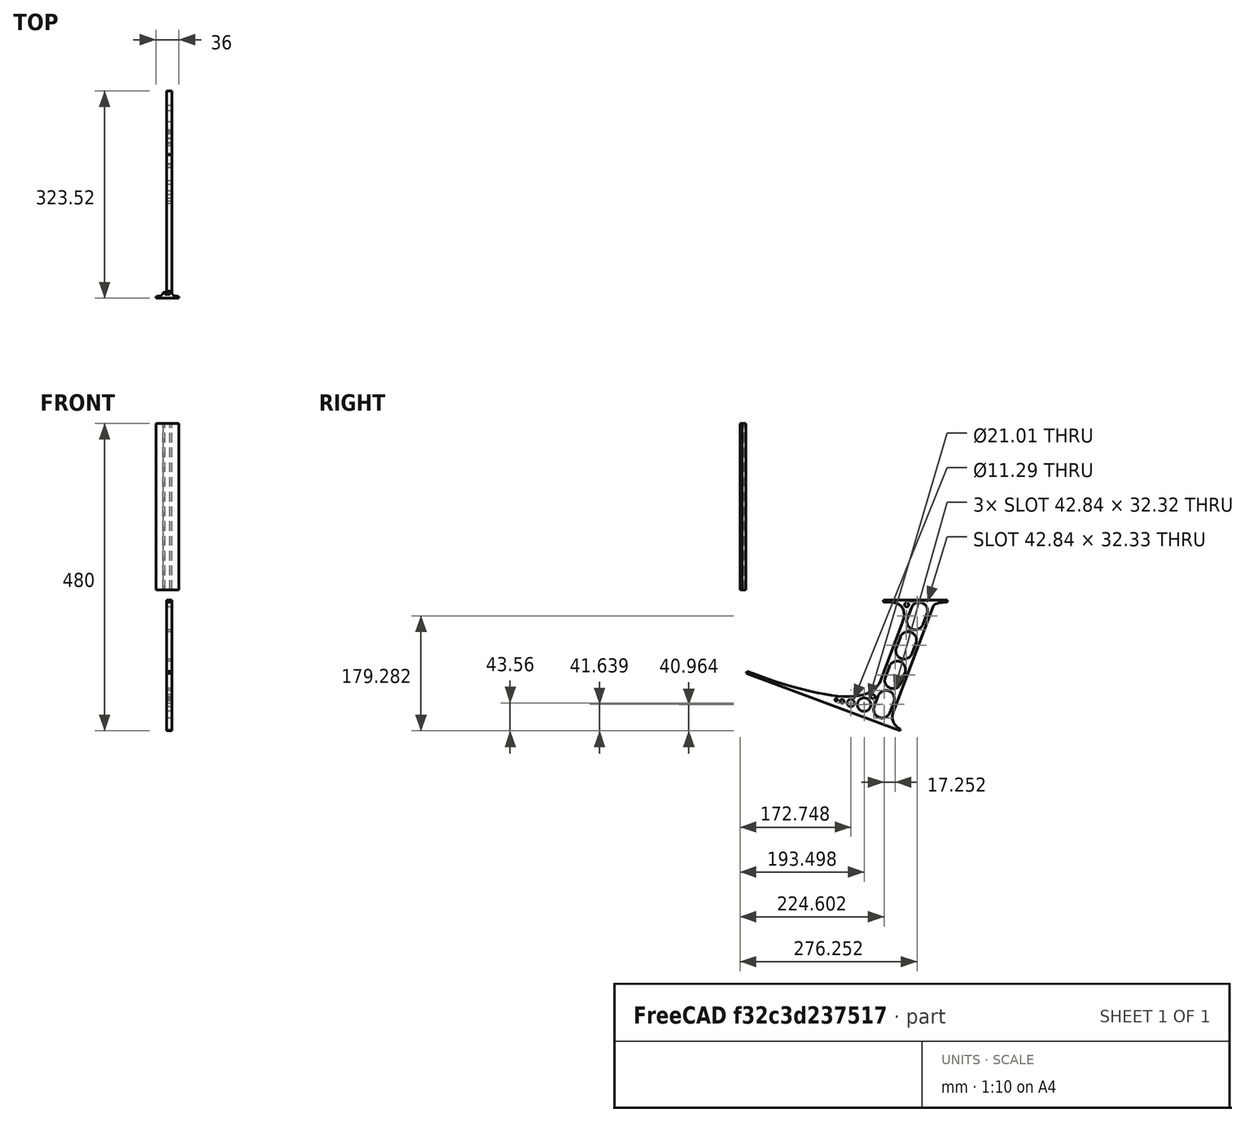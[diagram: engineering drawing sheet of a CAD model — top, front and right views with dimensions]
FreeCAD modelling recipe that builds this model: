
FCSTD DOCUMENT  (FreeCAD 0.19R0.19.2)
Label: laptopStand111
License: All rights reserved
LicenseURL: http://en.wikipedia.org/wiki/All_rights_reserved
objects: Sketcher::SketchObject×3, Part::Extrusion×3
note: 6 computed .brp shape members not serialized (recipe doc carries the construction recipe); baked Part::Feature solids carry a one-line shape summary decoded from their .brp

FEATURE [Sketcher::SketchObject] Sketch
  FullyConstrained = true
  sketch-geometry (316):
    g0: LineSegment StartX=-10.9272 StartY=-82.7794 StartZ=0 EndX=46.0728 EndY=-51.4823 EndZ=0
    g1: LineSegment StartX=-10.9272 StartY=77.3346 StartZ=0 EndX=-10.9272 EndY=-82.7794 EndZ=0
    g2: LineSegment StartX=-1.92719 StartY=-91.7794 StartZ=0 EndX=46.0728 EndY=-91.7794 EndZ=0
    g3: LineSegment StartX=318.073 StartY=-65.424 StartZ=0 EndX=318.073 EndY=-91.7794 EndZ=0
    g4: LineSegment StartX=318.073 StartY=-91.7794 StartZ=0 EndX=366.073 EndY=-91.7794 EndZ=0
    g5: LineSegment StartX=46.0728 StartY=-65.424 StartZ=0 EndX=-1.92719 EndY=-91.7794 EndZ=0
    g6: LineSegment StartX=46.0728 StartY=-65.424 StartZ=0 EndX=46.0728 EndY=-91.7794 EndZ=0
    g7: LineSegment StartX=46.0728 StartY=77.3346 StartZ=0 EndX=46.0728 EndY=-51.4823 EndZ=0
    g8: LineSegment StartX=-42.9272 StartY=136.221 StartZ=0 EndX=-42.9272 EndY=-103.779 EndZ=0
    g9: LineSegment StartX=407.073 StartY=136.221 StartZ=0 EndX=407.073 EndY=-103.779 EndZ=0
    g10: ArcOfCircle CenterX=-26.9272 CenterY=22.1087 CenterZ=0 NormalX=0 NormalY=0 NormalZ=1 AngleXU=0 Radius=8 StartAngle=1e-16 EndAngle=3.14159
    g11: ArcOfCircle CenterX=-26.9272 CenterY=-83.7794 CenterZ=0 NormalX=0 NormalY=0 NormalZ=1 AngleXU=0 Radius=8 StartAngle=3.14159 EndAngle=6.28319
    g12: LineSegment StartX=-34.9272 StartY=22.1087 StartZ=0 EndX=-34.9272 EndY=-83.7794 EndZ=0
    g13: LineSegment StartX=-18.9272 StartY=22.1087 StartZ=0 EndX=-18.9272 EndY=-83.7794 EndZ=0
    g14: ArcOfCircle CenterX=391.073 CenterY=22.1087 CenterZ=0 NormalX=0 NormalY=0 NormalZ=1 AngleXU=0 Radius=8 StartAngle=-4.4e-15 EndAngle=3.14159
    g15: LineSegment StartX=399.073 StartY=22.1087 StartZ=0 EndX=399.073 EndY=-83.7794 EndZ=0
    g16: LineSegment StartX=383.073 StartY=22.1087 StartZ=0 EndX=383.073 EndY=-83.7794 EndZ=0
    g17: ArcOfCircle CenterX=391.073 CenterY=-83.7794 CenterZ=0 NormalX=0 NormalY=0 NormalZ=1 AngleXU=0 Radius=8 StartAngle=3.14159 EndAngle=6.28319
    g18: Circle CenterX=175.022 CenterY=27.0628 CenterZ=0 NormalX=0 NormalY=0 NormalZ=1 AngleXU=0 Radius=1
    g19: Circle CenterX=179.022 CenterY=24.8665 CenterZ=0 NormalX=0 NormalY=0 NormalZ=1 AngleXU=0 Radius=1
    g20: Circle CenterX=179.022 CenterY=27.0628 CenterZ=0 NormalX=0 NormalY=0 NormalZ=1 AngleXU=0 Radius=1
    g21: BSplineCurve PolesCount=3 KnotsCount=2 Degree=2 IsPeriodic=0
    g22: GeomPoint X=175.022 Y=27.0628 Z=0
    g23: GeomPoint X=179.022 Y=27.0628 Z=0
    g24: Circle CenterX=189.124 CenterY=27.0628 CenterZ=0 NormalX=0 NormalY=0 NormalZ=1 AngleXU=0 Radius=1
    g25: Circle CenterX=185.124 CenterY=24.8665 CenterZ=0 NormalX=0 NormalY=0 NormalZ=1 AngleXU=0 Radius=1
    g26: Circle CenterX=185.124 CenterY=27.0628 CenterZ=0 NormalX=0 NormalY=0 NormalZ=1 AngleXU=0 Radius=1
    g27: BSplineCurve PolesCount=3 KnotsCount=2 Degree=2 IsPeriodic=0
    g28: GeomPoint X=189.124 Y=27.0628 Z=0
    g29: GeomPoint X=185.124 Y=27.0628 Z=0
    g30: Circle CenterX=175.022 CenterY=5.37834 CenterZ=0 NormalX=0 NormalY=0 NormalZ=1 AngleXU=0 Radius=1
    g31: Circle CenterX=179.022 CenterY=7.57463 CenterZ=0 NormalX=0 NormalY=0 NormalZ=1 AngleXU=0 Radius=1
    g32: Circle CenterX=179.022 CenterY=5.34704 CenterZ=0 NormalX=0 NormalY=0 NormalZ=1 AngleXU=0 Radius=1
    g33: BSplineCurve PolesCount=3 KnotsCount=2 Degree=2 IsPeriodic=0
    g34: GeomPoint X=175.022 Y=5.37834 Z=0
    g35: GeomPoint X=179.022 Y=5.34704 Z=0
    g36: Circle CenterX=189.124 CenterY=5.37834 CenterZ=0 NormalX=0 NormalY=0 NormalZ=1 AngleXU=0 Radius=1
    g37: Circle CenterX=185.124 CenterY=7.57463 CenterZ=0 NormalX=0 NormalY=0 NormalZ=1 AngleXU=0 Radius=1
    g38: Circle CenterX=185.124 CenterY=5.34704 CenterZ=0 NormalX=0 NormalY=0 NormalZ=1 AngleXU=0 Radius=1
    g39: BSplineCurve PolesCount=3 KnotsCount=2 Degree=2 IsPeriodic=0
    g40: GeomPoint X=189.124 Y=5.37834 Z=0
    g41: GeomPoint X=185.124 Y=5.34704 Z=0
    g42: Circle CenterX=165.871 CenterY=18.1458 CenterZ=0 NormalX=0 NormalY=0 NormalZ=1 AngleXU=0 Radius=1
    g43: Circle CenterX=169.377 CenterY=16.2206 CenterZ=0 NormalX=0 NormalY=0 NormalZ=1 AngleXU=0 Radius=1
    g44: Circle CenterX=165.871 CenterY=14.2954 CenterZ=0 NormalX=0 NormalY=0 NormalZ=1 AngleXU=0 Radius=1
    g45: BSplineCurve PolesCount=3 KnotsCount=2 Degree=2 IsPeriodic=0
    g46: GeomPoint X=165.871 Y=18.1458 Z=0
    g47: GeomPoint X=165.871 Y=14.2954 Z=0
    g48: Circle CenterX=198.275 CenterY=18.1458 CenterZ=0 NormalX=0 NormalY=0 NormalZ=1 AngleXU=0 Radius=1
    g49: Circle CenterX=194.768 CenterY=16.2206 CenterZ=0 NormalX=0 NormalY=0 NormalZ=1 AngleXU=0 Radius=1
    g50: Circle CenterX=198.275 CenterY=14.2954 CenterZ=0 NormalX=0 NormalY=0 NormalZ=1 AngleXU=0 Radius=1
    g51: BSplineCurve PolesCount=3 KnotsCount=2 Degree=2 IsPeriodic=0
    g52: GeomPoint X=198.275 Y=18.1458 Z=0
    g53: GeomPoint X=198.275 Y=14.2954 Z=0
    g54: LineSegment StartX=407.073 StartY=-103.779 StartZ=0 EndX=-42.9272 EndY=-103.779 EndZ=0
    g55: LineSegment StartX=407.073 StartY=136.221 StartZ=0 EndX=-42.9272 EndY=136.221 EndZ=0
    g56: LineSegment StartX=46.0728 StartY=77.3346 StartZ=0 EndX=-10.9272 EndY=77.3346 EndZ=0
    g57: LineSegment StartX=46.0728 StartY=105.865 StartZ=0 EndX=31.5028 EndY=105.865 EndZ=0
    g58: LineSegment StartX=46.0728 StartY=124.221 StartZ=0 EndX=46.0728 EndY=105.865 EndZ=0
    g59: LineSegment StartX=-1.92719 StartY=124.221 StartZ=0 EndX=31.5028 EndY=105.865 EndZ=0
    g60: LineSegment StartX=46.0728 StartY=124.221 StartZ=0 EndX=-1.92719 EndY=124.221 EndZ=0
    g61: Circle CenterX=125.607 CenterY=54.1951 CenterZ=0 NormalX=0 NormalY=0 NormalZ=1 AngleXU=0 Radius=1
    g62: Circle CenterX=139.632 CenterY=46.4944 CenterZ=0 NormalX=0 NormalY=0 NormalZ=1 AngleXU=0 Radius=1
    g63: Circle CenterX=127.326 CenterY=56.7187 CenterZ=0 NormalX=0 NormalY=0 NormalZ=1 AngleXU=0 Radius=1
    g64: BSplineCurve PolesCount=3 KnotsCount=2 Degree=2 IsPeriodic=0
    g65: GeomPoint X=125.607 Y=54.1951 Z=0
    g66: GeomPoint X=127.326 Y=56.7187 Z=0
    g67: Circle CenterX=236.821 CenterY=56.7187 CenterZ=0 NormalX=0 NormalY=0 NormalZ=1 AngleXU=0 Radius=1
    g68: Circle CenterX=224.513 CenterY=46.4944 CenterZ=0 NormalX=0 NormalY=0 NormalZ=1 AngleXU=0 Radius=1
    g69: Circle CenterX=238.538 CenterY=54.1951 CenterZ=0 NormalX=0 NormalY=0 NormalZ=1 AngleXU=0 Radius=1
    g70: BSplineCurve PolesCount=3 KnotsCount=2 Degree=2 IsPeriodic=0
    g71: GeomPoint X=236.821 Y=56.7187 Z=0
    g72: GeomPoint X=238.538 Y=54.1951 Z=0
    g73: Circle CenterX=238.538 CenterY=-21.7539 CenterZ=0 NormalX=0 NormalY=0 NormalZ=1 AngleXU=0 Radius=1
    g74: Circle CenterX=224.513 CenterY=-14.0532 CenterZ=0 NormalX=0 NormalY=0 NormalZ=1 AngleXU=0 Radius=1
    g75: Circle CenterX=236.821 CenterY=-24.2775 CenterZ=0 NormalX=0 NormalY=0 NormalZ=1 AngleXU=0 Radius=1
    g76: BSplineCurve PolesCount=3 KnotsCount=2 Degree=2 IsPeriodic=0
    g77: GeomPoint X=238.538 Y=-21.7539 Z=0
    g78: GeomPoint X=236.821 Y=-24.2775 Z=0
    g79: Circle CenterX=125.607 CenterY=-21.7539 CenterZ=0 NormalX=0 NormalY=0 NormalZ=1 AngleXU=0 Radius=1
    g80: Circle CenterX=139.632 CenterY=-14.0532 CenterZ=0 NormalX=0 NormalY=0 NormalZ=1 AngleXU=0 Radius=1
    g81: Circle CenterX=127.325 CenterY=-24.2775 CenterZ=0 NormalX=0 NormalY=0 NormalZ=1 AngleXU=0 Radius=1
    g82: BSplineCurve PolesCount=3 KnotsCount=2 Degree=2 IsPeriodic=0
    g83: GeomPoint X=125.607 Y=-21.7539 Z=0
    g84: GeomPoint X=127.325 Y=-24.2775 Z=0
    g85: Circle CenterX=302.996 CenterY=111.695 CenterZ=0 NormalX=0 NormalY=0 NormalZ=1 AngleXU=0 Radius=1
    g86: Circle CenterX=306.073 CenterY=114.251 CenterZ=0 NormalX=0 NormalY=0 NormalZ=1 AngleXU=0 Radius=1
    g87: Circle CenterX=306.073 CenterY=110.251 CenterZ=0 NormalX=0 NormalY=0 NormalZ=1 AngleXU=0 Radius=1
    g88: BSplineCurve PolesCount=3 KnotsCount=2 Degree=2 IsPeriodic=0
    g89: GeomPoint X=302.996 Y=111.695 Z=0
    g90: GeomPoint X=306.073 Y=110.251 Z=0
    g91: Circle CenterX=306.073 CenterY=95.2763 CenterZ=0 NormalX=0 NormalY=0 NormalZ=1 AngleXU=0 Radius=1
    g92: Circle CenterX=306.073 CenterY=91.2763 CenterZ=0 NormalX=0 NormalY=0 NormalZ=1 AngleXU=0 Radius=1
    g93: Circle CenterX=302.567 CenterY=89.3511 CenterZ=0 NormalX=0 NormalY=0 NormalZ=1 AngleXU=0 Radius=1
    g94: BSplineCurve PolesCount=3 KnotsCount=2 Degree=2 IsPeriodic=0
    g95: GeomPoint X=306.073 Y=95.2763 Z=0
    g96: GeomPoint X=302.567 Y=89.3511 Z=0
    g97: LineSegment StartX=306.073 StartY=110.251 StartZ=0 EndX=306.073 EndY=95.2763 EndZ=0
    g98: LineSegment StartX=302.996 StartY=111.695 StartZ=0 EndX=236.821 EndY=56.7187 EndZ=0
    g99: LineSegment StartX=238.538 StartY=54.1951 StartZ=0 EndX=302.567 EndY=89.3511 EndZ=0
    g100: Circle CenterX=61.1496 CenterY=111.695 CenterZ=0 NormalX=0 NormalY=0 NormalZ=1 AngleXU=0 Radius=1
    g101: Circle CenterX=58.0728 CenterY=114.251 CenterZ=0 NormalX=0 NormalY=0 NormalZ=1 AngleXU=0 Radius=1
    g102: Circle CenterX=58.0728 CenterY=110.251 CenterZ=0 NormalX=0 NormalY=0 NormalZ=1 AngleXU=0 Radius=1
    g103: BSplineCurve PolesCount=3 KnotsCount=2 Degree=2 IsPeriodic=0
    g104: GeomPoint X=61.1496 Y=111.695 Z=0
    g105: GeomPoint X=58.0728 Y=110.251 Z=0
    g106: Circle CenterX=61.5791 CenterY=89.3511 CenterZ=0 NormalX=0 NormalY=0 NormalZ=1 AngleXU=0 Radius=1
    g107: Circle CenterX=58.0728 CenterY=91.2763 CenterZ=0 NormalX=0 NormalY=0 NormalZ=1 AngleXU=0 Radius=1
    g108: Circle CenterX=58.0728 CenterY=95.2763 CenterZ=0 NormalX=0 NormalY=0 NormalZ=1 AngleXU=0 Radius=1
    g109: BSplineCurve PolesCount=3 KnotsCount=2 Degree=2 IsPeriodic=0
    g110: GeomPoint X=61.5791 Y=89.3511 Z=0
    g111: GeomPoint X=58.0728 Y=95.2763 Z=0
    g112: LineSegment StartX=58.0728 StartY=110.251 StartZ=0 EndX=58.0728 EndY=95.2763 EndZ=0
    g113: LineSegment StartX=61.1496 StartY=111.695 StartZ=0 EndX=127.326 EndY=56.7187 EndZ=0
    g114: LineSegment StartX=125.607 StartY=54.1951 StartZ=0 EndX=61.5791 EndY=89.3511 EndZ=0
    g115: Circle CenterX=61.5791 CenterY=-56.9099 CenterZ=0 NormalX=0 NormalY=0 NormalZ=1 AngleXU=0 Radius=1
    g116: Circle CenterX=58.0728 CenterY=-58.8351 CenterZ=0 NormalX=0 NormalY=0 NormalZ=1 AngleXU=0 Radius=1
    g117: Circle CenterX=58.0728 CenterY=-62.8351 CenterZ=0 NormalX=0 NormalY=0 NormalZ=1 AngleXU=0 Radius=1
    g118: BSplineCurve PolesCount=3 KnotsCount=2 Degree=2 IsPeriodic=0
    g119: GeomPoint X=61.5791 Y=-56.9099 Z=0
    g120: GeomPoint X=58.0728 Y=-62.8351 Z=0
    g121: Circle CenterX=58.0728 CenterY=-77.8102 CenterZ=0 NormalX=0 NormalY=0 NormalZ=1 AngleXU=0 Radius=1
    g122: Circle CenterX=58.0728 CenterY=-81.8102 CenterZ=0 NormalX=0 NormalY=0 NormalZ=1 AngleXU=0 Radius=1
    g123: Circle CenterX=61.1496 CenterY=-79.2541 CenterZ=0 NormalX=0 NormalY=0 NormalZ=1 AngleXU=0 Radius=1
    g124: BSplineCurve PolesCount=3 KnotsCount=2 Degree=2 IsPeriodic=0
    g125: GeomPoint X=58.0728 Y=-77.8102 Z=0
    g126: GeomPoint X=61.1496 Y=-79.2541 Z=0
    g127: LineSegment StartX=58.0728 StartY=-62.8351 StartZ=0 EndX=58.0728 EndY=-77.8102 EndZ=0
    g128: LineSegment StartX=61.1496 StartY=-79.2541 StartZ=0 EndX=127.325 EndY=-24.2775 EndZ=0
    g129: LineSegment StartX=125.607 StartY=-21.7539 StartZ=0 EndX=61.5791 EndY=-56.9099 EndZ=0
    g130: Circle CenterX=302.567 CenterY=-56.9099 CenterZ=0 NormalX=0 NormalY=0 NormalZ=1 AngleXU=0 Radius=1
    g131: Circle CenterX=306.073 CenterY=-58.8351 CenterZ=0 NormalX=0 NormalY=0 NormalZ=1 AngleXU=0 Radius=1
    g132: Circle CenterX=306.073 CenterY=-62.8351 CenterZ=0 NormalX=0 NormalY=0 NormalZ=1 AngleXU=0 Radius=1
    g133: BSplineCurve PolesCount=3 KnotsCount=2 Degree=2 IsPeriodic=0
    g134: GeomPoint X=302.567 Y=-56.9099 Z=0
    g135: GeomPoint X=306.073 Y=-62.8351 Z=0
    g136: Circle CenterX=302.996 CenterY=-79.2541 CenterZ=0 NormalX=0 NormalY=0 NormalZ=1 AngleXU=0 Radius=1
    g137: Circle CenterX=306.073 CenterY=-81.8102 CenterZ=0 NormalX=0 NormalY=0 NormalZ=1 AngleXU=0 Radius=1
    g138: Circle CenterX=306.073 CenterY=-77.8102 CenterZ=0 NormalX=0 NormalY=0 NormalZ=1 AngleXU=0 Radius=1
    g139: BSplineCurve PolesCount=3 KnotsCount=2 Degree=2 IsPeriodic=0
    g140: GeomPoint X=302.996 Y=-79.2541 Z=0
    g141: GeomPoint X=306.073 Y=-77.8102 Z=0
    g142: LineSegment StartX=306.073 StartY=-62.8351 StartZ=0 EndX=306.073 EndY=-77.8102 EndZ=0
    g143: LineSegment StartX=302.996 StartY=-79.2541 StartZ=0 EndX=236.821 EndY=-24.2775 EndZ=0
    g144: LineSegment StartX=238.538 StartY=-21.7539 StartZ=0 EndX=302.567 EndY=-56.9099 EndZ=0
    g145: Circle CenterX=61.6457 CenterY=-88.8112 CenterZ=0 NormalX=0 NormalY=0 NormalZ=1 AngleXU=0 Radius=1
    g146: Circle CenterX=58.0728 CenterY=-91.7794 CenterZ=0 NormalX=0 NormalY=0 NormalZ=1 AngleXU=0 Radius=1
    g147: Circle CenterX=63.9135 CenterY=-91.7794 CenterZ=0 NormalX=0 NormalY=0 NormalZ=1 AngleXU=0 Radius=1
    g148: BSplineCurve PolesCount=3 KnotsCount=2 Degree=2 IsPeriodic=0
    g149: GeomPoint X=61.6457 Y=-88.8112 Z=0
    g150: GeomPoint X=63.9135 Y=-91.7794 Z=0
    g151: Circle CenterX=179.022 CenterY=-85.8163 CenterZ=0 NormalX=0 NormalY=0 NormalZ=1 AngleXU=0 Radius=1
    g152: Circle CenterX=179.022 CenterY=-91.7794 CenterZ=0 NormalX=0 NormalY=0 NormalZ=1 AngleXU=0 Radius=1
    g153: Circle CenterX=171.895 CenterY=-91.7794 CenterZ=0 NormalX=0 NormalY=0 NormalZ=1 AngleXU=0 Radius=1
    g154: BSplineCurve PolesCount=3 KnotsCount=2 Degree=2 IsPeriodic=0
    g155: GeomPoint X=179.022 Y=-85.8163 Z=0
    g156: GeomPoint X=171.895 Y=-91.7794 Z=0
    g157: Circle CenterX=185.124 CenterY=-86.2028 CenterZ=0 NormalX=0 NormalY=0 NormalZ=1 AngleXU=0 Radius=1
    g158: Circle CenterX=185.124 CenterY=-91.7794 CenterZ=0 NormalX=0 NormalY=0 NormalZ=1 AngleXU=0 Radius=1
    g159: Circle CenterX=191.747 CenterY=-91.7794 CenterZ=0 NormalX=0 NormalY=0 NormalZ=1 AngleXU=0 Radius=1
    g160: BSplineCurve PolesCount=3 KnotsCount=2 Degree=2 IsPeriodic=0
    g161: GeomPoint X=185.124 Y=-86.2028 Z=0
    g162: GeomPoint X=191.747 Y=-91.7794 Z=0
    g163: Circle CenterX=299.888 CenterY=-86.6413 CenterZ=0 NormalX=0 NormalY=0 NormalZ=1 AngleXU=0 Radius=1
    g164: Circle CenterX=306.073 CenterY=-91.7794 CenterZ=0 NormalX=0 NormalY=0 NormalZ=1 AngleXU=0 Radius=1
    g165: Circle CenterX=298.776 CenterY=-91.7794 CenterZ=0 NormalX=0 NormalY=0 NormalZ=1 AngleXU=0 Radius=1
    g166: BSplineCurve PolesCount=3 KnotsCount=2 Degree=2 IsPeriodic=0
    g167: GeomPoint X=299.888 Y=-86.6413 Z=0
    g168: GeomPoint X=298.776 Y=-91.7794 Z=0
    g169: LineSegment StartX=189.124 StartY=5.37834 StartZ=0 EndX=299.888 EndY=-86.6413 EndZ=0
    g170: LineSegment StartX=298.776 StartY=-91.7794 StartZ=0 EndX=191.747 EndY=-91.7794 EndZ=0
    g171: LineSegment StartX=185.124 StartY=-86.2028 StartZ=0 EndX=185.124 EndY=5.34704 EndZ=0
    g172: LineSegment StartX=179.022 StartY=5.34704 StartZ=0 EndX=179.022 EndY=-85.8163 EndZ=0
    g173: LineSegment StartX=171.895 StartY=-91.7794 StartZ=0 EndX=63.9135 EndY=-91.7794 EndZ=0
    g174: LineSegment StartX=61.6457 StartY=-88.8112 StartZ=0 EndX=175.022 EndY=5.37834 EndZ=0
    g175: Circle CenterX=302.073 CenterY=124.221 CenterZ=0 NormalX=0 NormalY=0 NormalZ=1 AngleXU=0 Radius=1
    g176: Circle CenterX=306.073 CenterY=124.221 CenterZ=0 NormalX=0 NormalY=0 NormalZ=1 AngleXU=0 Radius=1
    g177: Circle CenterX=302.996 CenterY=121.665 CenterZ=0 NormalX=0 NormalY=0 NormalZ=1 AngleXU=0 Radius=1
    g178: BSplineCurve PolesCount=3 KnotsCount=2 Degree=2 IsPeriodic=0
    g179: GeomPoint X=302.073 Y=124.221 Z=0
    g180: GeomPoint X=302.996 Y=121.665 Z=0
    g181: Circle CenterX=189.124 CenterY=124.221 CenterZ=0 NormalX=0 NormalY=0 NormalZ=1 AngleXU=0 Radius=1
    g182: Circle CenterX=185.124 CenterY=124.221 CenterZ=0 NormalX=0 NormalY=0 NormalZ=1 AngleXU=0 Radius=1
    g183: Circle CenterX=185.124 CenterY=120.221 CenterZ=0 NormalX=0 NormalY=0 NormalZ=1 AngleXU=0 Radius=1
    g184: BSplineCurve PolesCount=3 KnotsCount=2 Degree=2 IsPeriodic=0
    g185: GeomPoint X=189.124 Y=124.221 Z=0
    g186: GeomPoint X=185.124 Y=120.221 Z=0
    g187: Circle CenterX=175.022 CenterY=124.221 CenterZ=0 NormalX=0 NormalY=0 NormalZ=1 AngleXU=0 Radius=1
    g188: Circle CenterX=179.022 CenterY=124.221 CenterZ=0 NormalX=0 NormalY=0 NormalZ=1 AngleXU=0 Radius=1
    g189: Circle CenterX=179.022 CenterY=120.221 CenterZ=0 NormalX=0 NormalY=0 NormalZ=1 AngleXU=0 Radius=1
    g190: BSplineCurve PolesCount=3 KnotsCount=2 Degree=2 IsPeriodic=0
    g191: GeomPoint X=175.022 Y=124.221 Z=0
    g192: GeomPoint X=179.022 Y=120.221 Z=0
    g193: Circle CenterX=62.0728 CenterY=124.221 CenterZ=0 NormalX=0 NormalY=0 NormalZ=1 AngleXU=0 Radius=1
    g194: Circle CenterX=58.0728 CenterY=124.221 CenterZ=0 NormalX=0 NormalY=0 NormalZ=1 AngleXU=0 Radius=1
    g195: Circle CenterX=61.1496 CenterY=121.665 CenterZ=0 NormalX=0 NormalY=0 NormalZ=1 AngleXU=0 Radius=1
    g196: BSplineCurve PolesCount=3 KnotsCount=2 Degree=2 IsPeriodic=0
    g197: GeomPoint X=62.0728 Y=124.221 Z=0
    g198: GeomPoint X=61.1496 Y=121.665 Z=0
    g199: LineSegment StartX=62.0728 StartY=124.221 StartZ=0 EndX=175.022 EndY=124.221 EndZ=0
    g200: LineSegment StartX=179.022 StartY=120.221 StartZ=0 EndX=179.022 EndY=27.0628 EndZ=0
    g201: LineSegment StartX=185.124 StartY=27.0628 StartZ=0 EndX=185.124 EndY=120.221 EndZ=0
    g202: LineSegment StartX=189.124 StartY=124.221 StartZ=0 EndX=302.073 EndY=124.221 EndZ=0
    g203: LineSegment StartX=302.996 StartY=121.665 StartZ=0 EndX=189.124 EndY=27.0628 EndZ=0
    g204: LineSegment StartX=175.022 StartY=27.0628 StartZ=0 EndX=61.1496 EndY=121.665 EndZ=0
    g205: Circle CenterX=61.5791 CenterY=75.4095 CenterZ=0 NormalX=0 NormalY=0 NormalZ=1 AngleXU=0 Radius=1
    g206: Circle CenterX=58.0728 CenterY=77.3346 CenterZ=0 NormalX=0 NormalY=0 NormalZ=1 AngleXU=0 Radius=1
    g207: Circle CenterX=58.0728 CenterY=73.3346 CenterZ=0 NormalX=0 NormalY=0 NormalZ=1 AngleXU=0 Radius=1
    g208: BSplineCurve PolesCount=3 KnotsCount=2 Degree=2 IsPeriodic=0
    g209: GeomPoint X=61.5791 Y=75.4095 Z=0
    g210: GeomPoint X=58.0728 Y=73.3346 Z=0
    g211: Circle CenterX=58.0728 CenterY=-40.8935 CenterZ=0 NormalX=0 NormalY=0 NormalZ=1 AngleXU=0 Radius=1
    g212: Circle CenterX=58.0728 CenterY=-44.8935 CenterZ=0 NormalX=0 NormalY=0 NormalZ=1 AngleXU=0 Radius=1
    g213: Circle CenterX=61.5791 CenterY=-42.9683 CenterZ=0 NormalX=0 NormalY=0 NormalZ=1 AngleXU=0 Radius=1
    g214: BSplineCurve PolesCount=3 KnotsCount=2 Degree=2 IsPeriodic=0
    g215: GeomPoint X=58.0728 Y=-40.8935 Z=0
    g216: GeomPoint X=61.5791 Y=-42.9683 Z=0
    g217: LineSegment StartX=61.5791 StartY=-42.9683 StartZ=0 EndX=165.871 EndY=14.2954 EndZ=0
    g218: LineSegment StartX=165.871 StartY=18.1458 StartZ=0 EndX=61.5791 EndY=75.4095 EndZ=0
    g219: LineSegment StartX=58.0728 StartY=73.3346 StartZ=0 EndX=58.0728 EndY=-40.8935 EndZ=0
    g220: Circle CenterX=302.567 CenterY=-42.9683 CenterZ=0 NormalX=0 NormalY=0 NormalZ=1 AngleXU=0 Radius=1
    g221: Circle CenterX=306.073 CenterY=-44.8935 CenterZ=0 NormalX=0 NormalY=0 NormalZ=1 AngleXU=0 Radius=1
    g222: Circle CenterX=306.073 CenterY=-40.8935 CenterZ=0 NormalX=0 NormalY=0 NormalZ=1 AngleXU=0 Radius=1
    g223: BSplineCurve PolesCount=3 KnotsCount=2 Degree=2 IsPeriodic=0
    g224: GeomPoint X=302.567 Y=-42.9683 Z=0
    g225: GeomPoint X=306.073 Y=-40.8935 Z=0
    g226: Circle CenterX=306.073 CenterY=73.3346 CenterZ=0 NormalX=0 NormalY=0 NormalZ=1 AngleXU=0 Radius=1
    g227: Circle CenterX=306.073 CenterY=77.3346 CenterZ=0 NormalX=0 NormalY=0 NormalZ=1 AngleXU=0 Radius=1
    g228: Circle CenterX=302.567 CenterY=75.4095 CenterZ=0 NormalX=0 NormalY=0 NormalZ=1 AngleXU=0 Radius=1
    g229: BSplineCurve PolesCount=3 KnotsCount=2 Degree=2 IsPeriodic=0
    g230: GeomPoint X=306.073 Y=73.3346 Z=0
    g231: GeomPoint X=302.567 Y=75.4095 Z=0
    g232: LineSegment StartX=302.567 StartY=-42.9683 StartZ=0 EndX=198.275 EndY=14.2954 EndZ=0
    g233: LineSegment StartX=198.275 StartY=18.1458 StartZ=0 EndX=302.567 EndY=75.4095 EndZ=0
    g234: LineSegment StartX=306.073 StartY=73.3346 StartZ=0 EndX=306.073 EndY=-40.8935 EndZ=0
    g235: LineSegment StartX=322.073 StartY=105.865 StartZ=0 EndX=328.643 EndY=105.865 EndZ=0
    g236: LineSegment StartX=318.073 StartY=120.221 StartZ=0 EndX=318.073 EndY=109.865 EndZ=0
    g237: LineSegment StartX=336.157 StartY=107.779 StartZ=0 EndX=362.567 EndY=122.294 EndZ=0
    g238: Circle CenterX=362.073 CenterY=124.221 CenterZ=0 NormalX=0 NormalY=0 NormalZ=1 AngleXU=0 Radius=1
    g239: Circle CenterX=366.073 CenterY=124.221 CenterZ=0 NormalX=0 NormalY=0 NormalZ=1 AngleXU=0 Radius=1
    g240: Circle CenterX=362.567 CenterY=122.294 CenterZ=0 NormalX=0 NormalY=0 NormalZ=1 AngleXU=0 Radius=1
    g241: BSplineCurve PolesCount=3 KnotsCount=2 Degree=2 IsPeriodic=0
    g242: GeomPoint X=362.073 Y=124.221 Z=0
    g243: GeomPoint X=362.567 Y=122.294 Z=0
    g244: Circle CenterX=322.073 CenterY=124.221 CenterZ=0 NormalX=0 NormalY=0 NormalZ=1 AngleXU=0 Radius=1
    g245: Circle CenterX=318.073 CenterY=124.221 CenterZ=0 NormalX=0 NormalY=0 NormalZ=1 AngleXU=0 Radius=1
    g246: Circle CenterX=318.073 CenterY=120.221 CenterZ=0 NormalX=0 NormalY=0 NormalZ=1 AngleXU=0 Radius=1
    g247: BSplineCurve PolesCount=3 KnotsCount=2 Degree=2 IsPeriodic=0
    g248: GeomPoint X=322.073 Y=124.221 Z=0
    g249: GeomPoint X=318.073 Y=120.221 Z=0
    g250: Circle CenterX=322.073 CenterY=105.865 CenterZ=0 NormalX=0 NormalY=0 NormalZ=1 AngleXU=0 Radius=1
    g251: Circle CenterX=318.073 CenterY=105.865 CenterZ=0 NormalX=0 NormalY=0 NormalZ=1 AngleXU=0 Radius=1
    g252: Circle CenterX=318.073 CenterY=109.865 CenterZ=0 NormalX=0 NormalY=0 NormalZ=1 AngleXU=0 Radius=1
    g253: BSplineCurve PolesCount=3 KnotsCount=2 Degree=2 IsPeriodic=0
    g254: GeomPoint X=322.073 Y=105.865 Z=0
    g255: GeomPoint X=318.073 Y=109.865 Z=0
    g256: Circle CenterX=336.157 CenterY=107.779 CenterZ=0 NormalX=0 NormalY=0 NormalZ=1 AngleXU=0 Radius=1
    g257: Circle CenterX=332.651 CenterY=105.853 CenterZ=0 NormalX=0 NormalY=0 NormalZ=1 AngleXU=0 Radius=1
    g258: Circle CenterX=328.643 CenterY=105.865 CenterZ=0 NormalX=0 NormalY=0 NormalZ=1 AngleXU=0 Radius=1
    g259: BSplineCurve PolesCount=3 KnotsCount=2 Degree=2 IsPeriodic=0
    g260: GeomPoint X=336.157 Y=107.779 Z=0
    g261: GeomPoint X=328.643 Y=105.865 Z=0
    g262: LineSegment StartX=322.073 StartY=124.221 StartZ=0 EndX=362.073 EndY=124.221 EndZ=0
    g263: Circle CenterX=371.567 CenterY=-80.8644 CenterZ=0 NormalX=0 NormalY=0 NormalZ=1 AngleXU=0 Radius=1
    g264: Circle CenterX=375.073 CenterY=-82.7896 CenterZ=0 NormalX=0 NormalY=0 NormalZ=1 AngleXU=0 Radius=1
    g265: Circle CenterX=375.073 CenterY=-78.7896 CenterZ=0 NormalX=0 NormalY=0 NormalZ=1 AngleXU=0 Radius=1
    g266: BSplineCurve PolesCount=3 KnotsCount=2 Degree=2 IsPeriodic=0
    g267: GeomPoint X=371.567 Y=-80.8644 Z=0
    g268: GeomPoint X=375.073 Y=-78.7896 Z=0
    g269: Circle CenterX=321.579 CenterY=-53.4075 CenterZ=0 NormalX=0 NormalY=0 NormalZ=1 AngleXU=0 Radius=1
    g270: Circle CenterX=318.073 CenterY=-51.4823 CenterZ=0 NormalX=0 NormalY=0 NormalZ=1 AngleXU=0 Radius=1
    g271: Circle CenterX=318.073 CenterY=-47.4823 CenterZ=0 NormalX=0 NormalY=0 NormalZ=1 AngleXU=0 Radius=1
    g272: BSplineCurve PolesCount=3 KnotsCount=2 Degree=2 IsPeriodic=0
    g273: GeomPoint X=321.579 Y=-53.4075 Z=0
    g274: GeomPoint X=318.073 Y=-47.4823 Z=0
    g275: Circle CenterX=318.073 CenterY=79.9235 CenterZ=0 NormalX=0 NormalY=0 NormalZ=1 AngleXU=0 Radius=1
    g276: Circle CenterX=318.073 CenterY=83.9235 CenterZ=0 NormalX=0 NormalY=0 NormalZ=1 AngleXU=0 Radius=1
    g277: Circle CenterX=322.073 CenterY=83.9235 CenterZ=0 NormalX=0 NormalY=0 NormalZ=1 AngleXU=0 Radius=1
    g278: BSplineCurve PolesCount=3 KnotsCount=2 Degree=2 IsPeriodic=0
    g279: GeomPoint X=318.073 Y=79.9235 Z=0
    g280: GeomPoint X=322.073 Y=83.9235 Z=0
    g281: Circle CenterX=375.073 CenterY=79.9235 CenterZ=0 NormalX=0 NormalY=0 NormalZ=1 AngleXU=0 Radius=1
    g282: Circle CenterX=375.073 CenterY=83.9235 CenterZ=0 NormalX=0 NormalY=0 NormalZ=1 AngleXU=0 Radius=1
    g283: Circle CenterX=371.073 CenterY=83.9235 CenterZ=0 NormalX=0 NormalY=0 NormalZ=1 AngleXU=0 Radius=1
    g284: BSplineCurve PolesCount=3 KnotsCount=2 Degree=2 IsPeriodic=0
    g285: GeomPoint X=375.073 Y=79.9235 Z=0
    g286: GeomPoint X=371.073 Y=83.9235 Z=0
    g287: LineSegment StartX=322.073 StartY=83.9235 StartZ=0 EndX=371.073 EndY=83.9235 EndZ=0
    g288: LineSegment StartX=375.073 StartY=79.9235 StartZ=0 EndX=375.073 EndY=-78.7896 EndZ=0
    g289: LineSegment StartX=371.567 StartY=-80.8644 StartZ=0 EndX=321.579 EndY=-53.4075 EndZ=0
    g290: LineSegment StartX=318.073 StartY=-47.4823 StartZ=0 EndX=318.073 EndY=79.9235 EndZ=0
    g291: LineSegment StartX=318.073 StartY=-65.424 StartZ=0 EndX=321.579 EndY=-67.3492 EndZ=0
    g292: LineSegment StartX=366.073 StartY=-91.7794 StartZ=0 EndX=362.567 EndY=-89.8542 EndZ=0
    g293: LineSegment StartX=366.073 StartY=-91.7794 StartZ=0 EndX=362.073 EndY=-91.7794 EndZ=0
    g294: LineSegment StartX=318.073 StartY=-91.7794 StartZ=0 EndX=322.073 EndY=-91.7794 EndZ=0
    g295: LineSegment StartX=318.073 StartY=-91.7794 StartZ=0 EndX=318.073 EndY=-87.7794 EndZ=0
    g296: LineSegment StartX=318.073 StartY=-65.424 StartZ=0 EndX=318.073 EndY=-69.424 EndZ=0
    g297: LineSegment StartX=318.073 StartY=-65.424 StartZ=0 EndX=366.073 EndY=-91.7794 EndZ=0
    g298: Circle CenterX=321.579 CenterY=-67.3492 CenterZ=0 NormalX=0 NormalY=0 NormalZ=1 AngleXU=0 Radius=1
    g299: Circle CenterX=318.073 CenterY=-65.424 CenterZ=0 NormalX=0 NormalY=0 NormalZ=1 AngleXU=0 Radius=1
    g300: Circle CenterX=318.073 CenterY=-69.424 CenterZ=0 NormalX=0 NormalY=0 NormalZ=1 AngleXU=0 Radius=1
    g301: BSplineCurve PolesCount=3 KnotsCount=2 Degree=2 IsPeriodic=0
    g302: GeomPoint X=321.579 Y=-67.3492 Z=0
    g303: GeomPoint X=318.073 Y=-69.424 Z=0
    g304: Circle CenterX=362.567 CenterY=-89.8542 CenterZ=0 NormalX=0 NormalY=0 NormalZ=1 AngleXU=0 Radius=1
    g305: Circle CenterX=366.073 CenterY=-91.7794 CenterZ=0 NormalX=0 NormalY=0 NormalZ=1 AngleXU=0 Radius=1
    g306: Circle CenterX=362.073 CenterY=-91.7794 CenterZ=0 NormalX=0 NormalY=0 NormalZ=1 AngleXU=0 Radius=1
    g307: BSplineCurve PolesCount=3 KnotsCount=2 Degree=2 IsPeriodic=0
    g308: GeomPoint X=362.567 Y=-89.8542 Z=0
    g309: GeomPoint X=362.073 Y=-91.7794 Z=0
    g310: Circle CenterX=322.073 CenterY=-91.7794 CenterZ=0 NormalX=0 NormalY=0 NormalZ=1 AngleXU=0 Radius=1
    g311: Circle CenterX=318.073 CenterY=-91.7794 CenterZ=0 NormalX=0 NormalY=0 NormalZ=1 AngleXU=0 Radius=1
    g312: Circle CenterX=318.073 CenterY=-87.7794 CenterZ=0 NormalX=0 NormalY=0 NormalZ=1 AngleXU=0 Radius=1
    g313: BSplineCurve PolesCount=3 KnotsCount=2 Degree=2 IsPeriodic=0
    g314: GeomPoint X=322.073 Y=-91.7794 Z=0
    g315: GeomPoint X=318.073 Y=-87.7794 Z=0
  constraints (539):
    c: Horizontal(g2)
    c: Coincident(g6,g5)
    c: Coincident(g0,g7)
    c: Block(g3)
    c: Block(g6)
    c: Block(g5)
    c: Block(g0)
    c: Block(g1)
    c: Block(g4)
    c: Block(g2)
    c: Vertical(g8)
    c: Vertical(g9)
    c: Block(g9)
    c: Block(g8)
    c: Tangent(g10,g13) = 1.5708
    c: Tangent(g10,g12) = -1.5708
    c: Tangent(g12,g11) = -1.5708
    c: Tangent(g13,g11) = 1.5708
    c: Vertical(g12)
    c: Equal(g10,g11)
    c: Block(g13)
    c: Block(g12)
    c: Tangent(g14,g15) = 1.5708
    c: Tangent(g15,g17) = 1.5708
    c: Equal(g14,g17)
    c: Coincident(g16,g14)
    c: Coincident(g16,g17)
    c: Block(g15)
    c: Block(g16)
    c: Weight(g18) = 1
    c: Equal(g18,g19)
    c: Equal(g18,g20)
    c: InternalAlignment(g18,g21)
    c: InternalAlignment(g19,g21)
    c: InternalAlignment(g20,g21)
    c: InternalAlignment(g22,g21)
    c: InternalAlignment(g23,g21)
    c: Weight(g24) = 1
    c: Equal(g24,g25)
    c: Equal(g24,g26)
    c: InternalAlignment(g24,g27)
    c: InternalAlignment(g25,g27)
    c: InternalAlignment(g26,g27)
    c: InternalAlignment(g28,g27)
    c: InternalAlignment(g29,g27)
    c: Block(g27)
    c: Block(g21)
    c: Weight(g30) = 1
    c: Equal(g30,g31)
    c: Equal(g30,g32)
    c: InternalAlignment(g30,g33)
    c: InternalAlignment(g31,g33)
    c: InternalAlignment(g32,g33)
    c: InternalAlignment(g34,g33)
    c: InternalAlignment(g35,g33)
    c: Weight(g36) = 1
    c: Equal(g36,g37)
    c: Equal(g36,g38)
    c: InternalAlignment(g36,g39)
    c: InternalAlignment(g37,g39)
    c: InternalAlignment(g38,g39)
    c: InternalAlignment(g40,g39)
    c: InternalAlignment(g41,g39)
    c: Block(g39)
    c: Block(g33)
    c: Weight(g42) = 1
    c: Equal(g42,g43)
    c: Equal(g42,g44)
    c: InternalAlignment(g42,g45)
    c: InternalAlignment(g43,g45)
    c: InternalAlignment(g44,g45)
    c: InternalAlignment(g46,g45)
    c: InternalAlignment(g47,g45)
    c: Weight(g48) = 1
    c: Equal(g48,g49)
    c: Equal(g48,g50)
    c: InternalAlignment(g48,g51)
    c: InternalAlignment(g49,g51)
    c: InternalAlignment(g50,g51)
    c: InternalAlignment(g52,g51)
    c: InternalAlignment(g53,g51)
    c: Block(g45)
    c: Block(g51)
    c: Coincident(g54,g9)
    c: Coincident(g54,g8)
    c: Horizontal(g54)
    c: Distance(g54) = 450
    c: Coincident(g55,g9)
    c: Coincident(g55,g8)
    c: Horizontal(g55)
    c: Horizontal(g56)
    c: Coincident(g7,g56)
    c: Horizontal(g57)
    c: Vertical(g58)
    c: Block(g58)
    c: Block(g57)
    c: Block(g56)
    c: Distance(g58) = 18.3554
    c: Coincident(g60,g58)
    c: Coincident(g60,g59)
    c: Horizontal(g60)
    c: Block(g60)
    c: Block(g59)
    c: Coincident(g57,g59)
    c: Coincident(g1,g56)
    c: Weight(g61) = 1
    c: Equal(g61,g62)
    c: Equal(g61,g63)
    c: InternalAlignment(g61,g64)
    c: InternalAlignment(g62,g64)
    c: InternalAlignment(g63,g64)
    c: InternalAlignment(g65,g64)
    c: InternalAlignment(g66,g64)
    c: Block(g64)
    c: Weight(g67) = 1
    c: Equal(g67,g68)
    c: Equal(g67,g69)
    c: InternalAlignment(g67,g70)
    c: InternalAlignment(g68,g70)
    c: InternalAlignment(g69,g70)
    c: InternalAlignment(g71,g70)
    c: InternalAlignment(g72,g70)
    c: Block(g70)
    c: Weight(g73) = 1
    c: Equal(g73,g74)
    c: Equal(g73,g75)
    c: InternalAlignment(g73,g76)
    c: InternalAlignment(g74,g76)
    c: InternalAlignment(g75,g76)
    c: InternalAlignment(g77,g76)
    c: InternalAlignment(g78,g76)
    c: Block(g76)
    c: Weight(g79) = 1
    c: Equal(g79,g80)
    c: Equal(g79,g81)
    c: InternalAlignment(g79,g82)
    c: InternalAlignment(g80,g82)
    c: InternalAlignment(g81,g82)
    c: InternalAlignment(g83,g82)
    c: InternalAlignment(g84,g82)
    c: Block(g82)
    c: Weight(g85) = 1
    c: Equal(g85,g86)
    c: Equal(g85,g87)
    c: InternalAlignment(g85,g88)
    c: InternalAlignment(g86,g88)
    c: InternalAlignment(g87,g88)
    c: InternalAlignment(g89,g88)
    c: InternalAlignment(g90,g88)
    c: Weight(g91) = 1
    c: Equal(g91,g92)
    c: Equal(g91,g93)
    c: InternalAlignment(g91,g94)
    c: InternalAlignment(g92,g94)
    c: InternalAlignment(g93,g94)
    c: InternalAlignment(g95,g94)
    c: InternalAlignment(g96,g94)
    c: Block(g88)
    c: Block(g94)
    c: Coincident(g97,g88)
    c: Coincident(g97,g94)
    c: Vertical(g97)
    c: Coincident(g98,g88)
    c: Coincident(g98,g70)
    c: Coincident(g99,g70)
    c: Coincident(g99,g94)
    c: Weight(g100) = 1
    c: Equal(g100,g101)
    c: Equal(g100,g102)
    c: InternalAlignment(g100,g103)
    c: InternalAlignment(g101,g103)
    c: InternalAlignment(g102,g103)
    c: InternalAlignment(g104,g103)
    c: InternalAlignment(g105,g103)
    c: Weight(g106) = 1
    c: Equal(g106,g107)
    c: Equal(g106,g108)
    c: InternalAlignment(g106,g109)
    c: InternalAlignment(g107,g109)
    c: InternalAlignment(g108,g109)
    c: InternalAlignment(g110,g109)
    c: InternalAlignment(g111,g109)
    c: Block(g103)
    c: Block(g109)
    c: Coincident(g112,g103)
    c: Coincident(g112,g109)
    c: Vertical(g112)
    c: Coincident(g113,g103)
    c: Coincident(g113,g64)
    c: Coincident(g114,g64)
    c: Coincident(g114,g109)
    c: Weight(g115) = 1
    c: Equal(g115,g116)
    c: Equal(g115,g117)
    c: InternalAlignment(g115,g118)
    c: InternalAlignment(g116,g118)
    c: InternalAlignment(g117,g118)
    c: InternalAlignment(g119,g118)
    c: InternalAlignment(g120,g118)
    c: Weight(g121) = 1
    c: Equal(g121,g122)
    c: Equal(g121,g123)
    c: InternalAlignment(g121,g124)
    c: InternalAlignment(g122,g124)
    c: InternalAlignment(g123,g124)
    c: InternalAlignment(g125,g124)
    c: InternalAlignment(g126,g124)
    c: Block(g118)
    c: Block(g124)
    c: Coincident(g127,g118)
    c: Coincident(g127,g124)
    c: Vertical(g127)
    c: Coincident(g128,g124)
    c: Coincident(g128,g82)
    c: Coincident(g129,g82)
    c: Coincident(g129,g118)
    c: Weight(g130) = 1
    c: Equal(g130,g131)
    c: Equal(g130,g132)
    c: InternalAlignment(g130,g133)
    c: InternalAlignment(g131,g133)
    c: InternalAlignment(g132,g133)
    c: InternalAlignment(g134,g133)
    c: InternalAlignment(g135,g133)
    c: Weight(g136) = 1
    c: Equal(g136,g137)
    c: Equal(g136,g138)
    c: InternalAlignment(g136,g139)
    c: InternalAlignment(g137,g139)
    c: InternalAlignment(g138,g139)
    c: InternalAlignment(g140,g139)
    c: InternalAlignment(g141,g139)
    c: Block(g133)
    c: Block(g139)
    c: Coincident(g142,g133)
    c: Coincident(g142,g139)
    c: Vertical(g142)
    c: Coincident(g143,g139)
    c: Coincident(g143,g76)
    c: Coincident(g144,g76)
    c: Coincident(g144,g133)
    c: Weight(g145) = 1
    c: Equal(g145,g146)
    c: Equal(g145,g147)
    c: InternalAlignment(g145,g148)
    c: InternalAlignment(g146,g148)
    c: InternalAlignment(g147,g148)
    c: InternalAlignment(g149,g148)
    c: InternalAlignment(g150,g148)
    c: Weight(g151) = 1
    c: Equal(g151,g152)
    c: Equal(g151,g153)
    c: InternalAlignment(g151,g154)
    c: InternalAlignment(g152,g154)
    c: InternalAlignment(g153,g154)
    c: InternalAlignment(g155,g154)
    c: InternalAlignment(g156,g154)
    c: Weight(g157) = 1
    c: Equal(g157,g158)
    c: Equal(g157,g159)
    c: InternalAlignment(g157,g160)
    c: InternalAlignment(g158,g160)
    c: InternalAlignment(g159,g160)
    c: InternalAlignment(g161,g160)
    c: InternalAlignment(g162,g160)
    c: Weight(g163) = 1
    c: Equal(g163,g164)
    c: Equal(g163,g165)
    c: InternalAlignment(g163,g166)
    c: InternalAlignment(g164,g166)
    c: InternalAlignment(g165,g166)
    c: InternalAlignment(g167,g166)
    c: InternalAlignment(g168,g166)
    c: Block(g166)
    c: Block(g160)
    c: Block(g154)
    c: Block(g148)
    c: Coincident(g169,g39)
    c: Coincident(g169,g166)
    c: Coincident(g170,g166)
    c: Coincident(g170,g160)
    c: Horizontal(g170)
    c: Coincident(g171,g160)
    c: Coincident(g171,g39)
    c: Vertical(g171)
    c: Coincident(g172,g33)
    c: Coincident(g172,g154)
    c: Vertical(g172)
    c: Coincident(g173,g154)
    c: Coincident(g173,g148)
    c: Horizontal(g173)
    c: Coincident(g174,g148)
    c: Coincident(g174,g33)
    c: Weight(g175) = 1
    c: Equal(g175,g176)
    c: Equal(g175,g177)
    c: InternalAlignment(g175,g178)
    c: InternalAlignment(g176,g178)
    c: InternalAlignment(g177,g178)
    c: InternalAlignment(g179,g178)
    c: InternalAlignment(g180,g178)
    c: Weight(g181) = 1
    c: Equal(g181,g182)
    c: Equal(g181,g183)
    c: InternalAlignment(g181,g184)
    c: InternalAlignment(g182,g184)
    c: InternalAlignment(g183,g184)
    c: InternalAlignment(g185,g184)
    c: InternalAlignment(g186,g184)
    c: Weight(g187) = 1
    c: Equal(g187,g188)
    c: Equal(g187,g189)
    c: InternalAlignment(g187,g190)
    c: InternalAlignment(g188,g190)
    c: InternalAlignment(g189,g190)
    c: InternalAlignment(g191,g190)
    c: InternalAlignment(g192,g190)
    c: Weight(g193) = 1
    c: Equal(g193,g194)
    c: Equal(g193,g195)
    c: InternalAlignment(g193,g196)
    c: InternalAlignment(g194,g196)
    c: InternalAlignment(g195,g196)
    c: InternalAlignment(g197,g196)
    c: InternalAlignment(g198,g196)
    c: Block(g196)
    c: Block(g190)
    c: Block(g184)
    c: Block(g178)
    c: Coincident(g199,g196)
    c: Coincident(g199,g190)
    c: Horizontal(g199)
    c: Coincident(g200,g190)
    c: Coincident(g200,g21)
    c: Vertical(g200)
    c: Coincident(g201,g27)
    c: Coincident(g201,g184)
    c: Vertical(g201)
    c: Coincident(g202,g184)
    c: Coincident(g202,g178)
    c: Horizontal(g202)
    c: Coincident(g203,g178)
    c: Coincident(g203,g27)
    c: Coincident(g204,g21)
    c: Weight(g205) = 1
    c: Equal(g205,g206)
    c: Equal(g205,g207)
    c: InternalAlignment(g205,g208)
    c: InternalAlignment(g206,g208)
    c: InternalAlignment(g207,g208)
    c: InternalAlignment(g209,g208)
    c: InternalAlignment(g210,g208)
    c: Weight(g211) = 1
    c: Equal(g211,g212)
    c: Equal(g211,g213)
    c: InternalAlignment(g211,g214)
    c: InternalAlignment(g212,g214)
    c: InternalAlignment(g213,g214)
    c: InternalAlignment(g215,g214)
    c: InternalAlignment(g216,g214)
    c: Block(g214)
    c: Block(g208)
    c: Coincident(g217,g214)
    c: Coincident(g217,g45)
    c: Coincident(g218,g45)
    c: Coincident(g218,g208)
    c: Coincident(g219,g208)
    c: Coincident(g219,g214)
    c: Vertical(g219)
    c: Weight(g220) = 1
    c: Equal(g220,g221)
    c: Equal(g220,g222)
    c: InternalAlignment(g220,g223)
    c: InternalAlignment(g221,g223)
    c: InternalAlignment(g222,g223)
    c: InternalAlignment(g224,g223)
    c: InternalAlignment(g225,g223)
    c: Weight(g226) = 1
    c: Equal(g226,g227)
    c: Equal(g226,g228)
    c: InternalAlignment(g226,g229)
    c: InternalAlignment(g227,g229)
    c: InternalAlignment(g228,g229)
    c: InternalAlignment(g230,g229)
    c: InternalAlignment(g231,g229)
    c: Block(g229)
    c: Block(g223)
    c: Coincident(g232,g223)
    c: Coincident(g232,g51)
    c: Coincident(g233,g51)
    c: Coincident(g233,g229)
    c: Coincident(g234,g229)
    c: Coincident(g234,g223)
    c: Vertical(g234)
    c: Horizontal(g235)
    c: Block(g235)
    c: Vertical(g236)
    c: Block(g236)
    c: Block(g237)
    c: Weight(g238) = 1
    c: Equal(g238,g239)
    c: Equal(g238,g240)
    c: InternalAlignment(g238,g241)
    c: InternalAlignment(g239,g241)
    c: InternalAlignment(g240,g241)
    c: InternalAlignment(g242,g241)
    c: InternalAlignment(g243,g241)
    c: Weight(g244) = 1
    c: Equal(g244,g245)
    c: Equal(g244,g246)
    c: InternalAlignment(g244,g247)
    c: InternalAlignment(g245,g247)
    c: InternalAlignment(g246,g247)
    c: InternalAlignment(g248,g247)
    c: InternalAlignment(g249,g247)
    c: Weight(g250) = 1
    c: Equal(g250,g251)
    c: Equal(g250,g252)
    c: InternalAlignment(g250,g253)
    c: InternalAlignment(g251,g253)
    c: InternalAlignment(g252,g253)
    c: InternalAlignment(g254,g253)
    c: InternalAlignment(g255,g253)
    c: Weight(g256) = 1
    c: Equal(g256,g257)
    c: Equal(g256,g258)
    c: InternalAlignment(g256,g259)
    c: InternalAlignment(g257,g259)
    c: InternalAlignment(g258,g259)
    c: InternalAlignment(g260,g259)
    c: InternalAlignment(g261,g259)
    c: Block(g241)
    c: Block(g247)
    c: Block(g253)
    c: Block(g259)
    c: Coincident(g262,g247)
    c: Coincident(g262,g241)
    c: Horizontal(g262)
    c: Block(g204)
    c: Weight(g263) = 1
    c: Equal(g263,g264)
    c: Equal(g263,g265)
    c: InternalAlignment(g263,g266)
    c: InternalAlignment(g264,g266)
    c: InternalAlignment(g265,g266)
    c: InternalAlignment(g267,g266)
    c: InternalAlignment(g268,g266)
    c: Weight(g269) = 1
    c: Equal(g269,g270)
    c: Equal(g269,g271)
    c: InternalAlignment(g269,g272)
    c: InternalAlignment(g270,g272)
    c: InternalAlignment(g271,g272)
    c: InternalAlignment(g273,g272)
    c: InternalAlignment(g274,g272)
    c: Weight(g275) = 1
    c: Equal(g275,g276)
    c: Equal(g275,g277)
    c: InternalAlignment(g275,g278)
    c: InternalAlignment(g276,g278)
    c: InternalAlignment(g277,g278)
    c: InternalAlignment(g279,g278)
    c: InternalAlignment(g280,g278)
    c: Weight(g281) = 1
    c: Equal(g281,g282)
    c: Equal(g281,g283)
    c: InternalAlignment(g281,g284)
    c: InternalAlignment(g282,g284)
    c: InternalAlignment(g283,g284)
    c: InternalAlignment(g285,g284)
    c: InternalAlignment(g286,g284)
    c: Block(g266)
    c: Block(g272)
    c: Block(g278)
    c: Block(g284)
    c: Coincident(g287,g278)
    c: Coincident(g287,g284)
    c: Horizontal(g287)
    c: Coincident(g288,g284)
    c: Coincident(g288,g266)
    c: Vertical(g288)
    c: Coincident(g289,g266)
    c: Coincident(g289,g272)
    c: Coincident(g290,g272)
    c: Coincident(g290,g278)
    c: Vertical(g290)
    c: Horizontal(g293)
    c: Horizontal(g294)
    c: Vertical(g295)
    c: Vertical(g296)
    c: Distance(g296) = 4
    c: Distance(g291) = 4
    c: Distance(g295) = 4
    c: Distance(g294) = 4
    c: Distance(g293) = 4
    c: Distance(g292) = 4
    c: Coincident(g297,g3)
    c: Coincident(g297,g4)
    c: Parallel(g292,g297)
    c: Coincident(g292,g4)
    c: Coincident(g293,g4)
    c: Coincident(g294,g3)
    c: Coincident(g295,g3)
    c: Coincident(g296,g3)
    c: Coincident(g291,g3)
    c: Parallel(g297,g291)
    c: Coincident(g301,g291)
    c: Weight(g298) = 1
    c: Equal(g298,g299)
    c: Coincident(g299,g3)
    c: Equal(g298,g300)
    c: Coincident(g301,g296)
    c: InternalAlignment(g298,g301)
    c: InternalAlignment(g299,g301)
    c: InternalAlignment(g300,g301)
    c: InternalAlignment(g302,g301)
    c: InternalAlignment(g303,g301)
    c: Coincident(g307,g292)
    c: Weight(g304) = 1
    c: Equal(g304,g305)
    c: Coincident(g305,g4)
    c: Equal(g304,g306)
    c: Coincident(g307,g293)
    c: InternalAlignment(g304,g307)
    c: InternalAlignment(g305,g307)
    c: InternalAlignment(g306,g307)
    c: InternalAlignment(g308,g307)
    c: InternalAlignment(g309,g307)
    c: Coincident(g313,g294)
    c: Weight(g310) = 1
    c: Equal(g310,g311)
    c: Coincident(g311,g3)
    c: Equal(g310,g312)
    c: Coincident(g313,g295)
    c: InternalAlignment(g310,g313)
    c: InternalAlignment(g311,g313)
    c: InternalAlignment(g312,g313)
    c: InternalAlignment(g314,g313)
    c: InternalAlignment(g315,g313)
FEATURE [Sketcher::SketchObject] Sketch001
  FullyConstrained = true
  MapMode = 4
  Placement = pos=(0,0,0) rot=(0.57735,0.57735,0.57735;2.0944rad)
  Support = -> [Sketch]
  sketch-geometry (46):
    g0: BSplineCurve PolesCount=3 KnotsCount=2 Degree=2 IsPeriodic=0
    g1: ArcOfCircle CenterX=73.1223 CenterY=-32.291 CenterZ=0 NormalX=0 NormalY=0 NormalZ=1 AngleXU=0 Radius=13 StartAngle=5.92268 EndAngle=9.06428
    g2: ArcOfCircle CenterX=66.7816 CenterY=-49.1439 CenterZ=0 NormalX=0 NormalY=0 NormalZ=1 AngleXU=0 Radius=13 StartAngle=2.78068 EndAngle=5.92131
    g3: ArcOfCircle CenterX=55.9263 CenterY=-78.1807 CenterZ=0 NormalX=0 NormalY=0 NormalZ=1 AngleXU=0 Radius=13 StartAngle=5.92268 EndAngle=9.06428
    g4: ArcOfCircle CenterX=49.5884 CenterY=-95.0342 CenterZ=0 NormalX=0 NormalY=0 NormalZ=1 AngleXU=0 Radius=13 StartAngle=2.78068 EndAngle=5.92131
    g5: ArcOfCircle CenterX=38.7206 CenterY=-124.067 CenterZ=0 NormalX=0 NormalY=0 NormalZ=1 AngleXU=0 Radius=13 StartAngle=5.92268 EndAngle=9.06428
    g6: ArcOfCircle CenterX=32.3875 CenterY=-140.92 CenterZ=0 NormalX=0 NormalY=0 NormalZ=1 AngleXU=0 Radius=13 StartAngle=2.78068 EndAngle=5.92131
    g7: ArcOfCircle CenterX=21.4715 CenterY=-169.934 CenterZ=0 NormalX=0 NormalY=0 NormalZ=1 AngleXU=0 Radius=13 StartAngle=5.92268 EndAngle=9.06428
    g8: ArcOfCircle CenterX=15.1336 CenterY=-186.787 CenterZ=0 NormalX=0 NormalY=0 NormalZ=1 AngleXU=0 Radius=13 StartAngle=2.78068 EndAngle=5.92131
    g9-g12: Circle x4 (B-spline internal-alignment scaffolding for g13; pole/knot coordinates omitted)
    g13: BSplineCurve PolesCount=4 KnotsCount=2 Degree=3 IsPeriodic=0
    g14: GeomPoint X=28.8094 Y=-19.0875 Z=0
    g15: GeomPoint X=47.0443 Y=-50.4712 Z=0
    g16: Circle CenterX=53.5586 CenterY=-23.2695 CenterZ=0 NormalX=0 NormalY=0 NormalZ=1 AngleXU=0 Radius=3.24518
    g17: Circle CenterX=-195.441 CenterY=-127.082 CenterZ=0 NormalX=0 NormalY=0 NormalZ=1 AngleXU=0 Radius=1
    g18: Circle CenterX=-8.24091 CenterY=-197.481 CenterZ=0 NormalX=0 NormalY=0 NormalZ=1 AngleXU=0 Radius=1
    g19: Circle CenterX=12.8789 CenterY=-141.321 CenterZ=0 NormalX=0 NormalY=0 NormalZ=1 AngleXU=0 Radius=1
    g20: BSplineCurve PolesCount=3 KnotsCount=2 Degree=2 IsPeriodic=0
    g21: GeomPoint X=-195.441 Y=-127.082 Z=0
    g22: GeomPoint X=12.8789 Y=-141.321 Z=0
    g23: Circle CenterX=-12.8016 CenterY=-179.036 CenterZ=0 NormalX=0 NormalY=0 NormalZ=1 AngleXU=0 Radius=10.5072
    g24: Circle CenterX=0.933922 CenterY=-166.43 CenterZ=0 NormalX=0 NormalY=0 NormalZ=1 AngleXU=0 Radius=3.26661
    g25: Circle CenterX=-33.5518 CenterY=-176.44 CenterZ=0 NormalX=0 NormalY=0 NormalZ=1 AngleXU=0 Radius=5.64388
    g26: Circle CenterX=-47.2366 CenterY=-173.859 CenterZ=0 NormalX=0 NormalY=0 NormalZ=1 AngleXU=0 Radius=3.01653
    g27: Circle CenterX=-56.2595 CenterY=-171.456 CenterZ=0 NormalX=0 NormalY=0 NormalZ=1 AngleXU=0 Radius=2.12826
    g28: ArcOfCircle CenterX=51.2151 CenterY=-198.473 CenterZ=0 NormalX=0 NormalY=0 NormalZ=1 AngleXU=0 Radius=20 StartAngle=2.78189 EndAngle=4.35269
    g29: LineSegment StartX=32.4951 StartY=-191.433 StartZ=0 EndX=94.6578 EndY=-26.1352 EndZ=0
    g30: LineSegment StartX=43.1192 StartY=-220.001 StartZ=0 EndX=-196.497 EndY=-129.89 EndZ=0
    g31: LineSegment StartX=43.1192 StartY=-220.001 StartZ=0 EndX=44.1752 EndY=-217.193 EndZ=0
    g32: LineSegment StartX=117.223 StartY=-19.0875 StartZ=0 EndX=117.223 EndY=-16.0875 EndZ=0
    g33: LineSegment StartX=117.223 StartY=-16.0875 StartZ=0 EndX=17.2232 EndY=-16.0875 EndZ=0
    g34: LineSegment StartX=17.2232 StartY=-16.0875 StartZ=0 EndX=17.2232 EndY=-19.0875 EndZ=0
    g35: LineSegment StartX=28.8094 StartY=-19.0875 StartZ=0 EndX=17.2232 EndY=-19.0875 EndZ=0
    g36: LineSegment StartX=47.0443 StartY=-50.4712 StartZ=0 EndX=12.8789 EndY=-141.321 EndZ=0
    g37: LineSegment StartX=-195.441 StartY=-127.082 StartZ=0 EndX=-196.497 EndY=-129.89 EndZ=0
    g38: LineSegment StartX=85.2866 StartY=-36.8766 StartZ=0 EndX=78.9396 EndY=-53.7463 EndZ=0
    g39: LineSegment StartX=60.9579 StartY=-27.7053 StartZ=0 EndX=54.6191 EndY=-44.5532 EndZ=0
    g40: LineSegment StartX=68.0907 StartY=-82.7664 StartZ=0 EndX=61.7465 EndY=-99.6365 EndZ=0
    g41: LineSegment StartX=43.7619 StartY=-73.595 StartZ=0 EndX=37.426 EndY=-90.4435 EndZ=0
    g42: LineSegment StartX=50.885 StartY=-128.652 StartZ=0 EndX=44.5456 EndY=-145.522 EndZ=0
    g43: LineSegment StartX=26.5562 StartY=-119.481 StartZ=0 EndX=20.2251 EndY=-136.329 EndZ=0
    g44: LineSegment StartX=9.3071 StartY=-165.349 StartZ=0 EndX=2.97115 EndY=-182.197 EndZ=0
    g45: LineSegment StartX=33.6358 StartY=-174.52 StartZ=0 EndX=27.2917 EndY=-191.39 EndZ=0
  constraints (71):
    c: Block(g0)
    c: Block(g1)
    c: Block(g2)
    c: Block(g4)
    c: Block(g3)
    c: Block(g6)
    c: Block(g5)
    c: Block(g8)
    c: Block(g7)
    c: Weight(g9) = 1
    c: Equal(g9,g10)
    c: Equal(g9,g11)
    c: Equal(g9,g12)
    c: InternalAlignment(g9-g12 -> g13) x4
    c: InternalAlignment(g14,g13)
    c: InternalAlignment(g15,g13)
    c: Block(g16)
    c: Weight(g17) = 1
    c: Equal(g17,g18)
    c: Equal(g17,g19)
    c: InternalAlignment(g17,g20)
    c: InternalAlignment(g18,g20)
    c: InternalAlignment(g19,g20)
    c: InternalAlignment(g21,g20)
    c: InternalAlignment(g22,g20)
    c: Block(g20)
    c: Block(g23)
    c: Block(g24)
    c: Block(g25)
    c: Block(g26)
    c: Block(g27)
    c: Block(g28)
    c: Coincident(g29,g28)
    c: Coincident(g29,g0)
    c: Block(g13)
    c: Coincident(g31,g30)
    c: Coincident(g31,g28)
    c: Block(g31)
    c: Coincident(g32,g0)
    c: Vertical(g32)
    c: Coincident(g33,g32)
    c: Horizontal(g33)
    c: Coincident(g34,g33)
    c: Vertical(g34)
    c: Block(g33)
    c: Coincident(g35,g13)
    c: Coincident(g35,g34)
    c: Horizontal(g35)
    c: Coincident(g36,g13)
    c: Coincident(g36,g20)
    c: Coincident(g37,g20)
    c: Coincident(g37,g30)
    c: Block(g30)
    c: Coincident(g38,g1)
    c: Coincident(g38,g2)
    c: Coincident(g39,g1)
    c: Coincident(g39,g2)
    c: Coincident(g40,g3)
    c: Coincident(g40,g4)
    c: Coincident(g41,g3)
    c: Coincident(g41,g4)
    c: Coincident(g42,g5)
    c: Coincident(g42,g6)
    c: Coincident(g43,g5)
    c: Coincident(g43,g6)
    c: Coincident(g44,g7)
    c: Coincident(g44,g8)
    c: Coincident(g45,g7)
    c: Coincident(g45,g8)
    c: Distance(g30) = 256
    c: Distance(g33) = 100
FEATURE [Part::Extrusion] Extrude002
  Base = -> Sketch001
  Dir = (1,0,0)
  DirMode = 2
  FaceMakerClass = Part::FaceMakerBullseye
  LengthFwd = 8
  LengthRev = 0
  Solid = true
  Symmetric = false
FEATURE [Sketcher::SketchObject] Sketch002
  FullyConstrained = true
  sketch-geometry (20):
    g0: LineSegment StartX=-2.77179 StartY=-200.304 StartZ=0 EndX=5.22821 EndY=-200.304 EndZ=0
    g1: LineSegment StartX=5.22821 StartY=-200.304 StartZ=0 EndX=5.22821 EndY=-197.304 EndZ=0
    g2: LineSegment StartX=-2.77179 StartY=-200.304 StartZ=0 EndX=-2.77179 EndY=-197.304 EndZ=0
    g3: LineSegment StartX=5.22821 StartY=-197.304 StartZ=0 EndX=8.22821 EndY=-197.304 EndZ=0
    g4: LineSegment StartX=-2.77179 StartY=-197.304 StartZ=0 EndX=-5.77179 EndY=-197.304 EndZ=0
    g5: LineSegment StartX=19.2282 StartY=-203.304 StartZ=0 EndX=19.2282 EndY=-206.304 EndZ=0
    g6: LineSegment StartX=-16.7718 StartY=-203.304 StartZ=0 EndX=-16.7718 EndY=-206.304 EndZ=0
    g7: LineSegment StartX=-16.7718 StartY=-206.304 StartZ=0 EndX=19.2282 EndY=-206.304 EndZ=0
    g8: Circle CenterX=-16.7718 CenterY=-203.304 CenterZ=0 NormalX=0 NormalY=0 NormalZ=1 AngleXU=0 Radius=1
    g9: Circle CenterX=-5.77179 CenterY=-203.304 CenterZ=0 NormalX=0 NormalY=0 NormalZ=1 AngleXU=0 Radius=1
    g10: Circle CenterX=-5.77179 CenterY=-197.304 CenterZ=0 NormalX=0 NormalY=0 NormalZ=1 AngleXU=0 Radius=1
    g11: BSplineCurve PolesCount=3 KnotsCount=2 Degree=2 IsPeriodic=0
    g12: GeomPoint X=-16.7718 Y=-203.304 Z=0
    g13: GeomPoint X=-5.77179 Y=-197.304 Z=0
    g14: Circle CenterX=19.2282 CenterY=-203.304 CenterZ=0 NormalX=0 NormalY=0 NormalZ=1 AngleXU=0 Radius=1
    g15: Circle CenterX=8.22821 CenterY=-203.304 CenterZ=0 NormalX=0 NormalY=0 NormalZ=1 AngleXU=0 Radius=1
    g16: Circle CenterX=8.22821 CenterY=-197.304 CenterZ=0 NormalX=0 NormalY=0 NormalZ=1 AngleXU=0 Radius=1
    g17: BSplineCurve PolesCount=3 KnotsCount=2 Degree=2 IsPeriodic=0
    g18: GeomPoint X=19.2282 Y=-203.304 Z=0
    g19: GeomPoint X=8.22821 Y=-197.304 Z=0
  constraints (41):
    c: Horizontal(g0)
    c: Distance(g0) = 8
    c: Coincident(g1,g0)
    c: Vertical(g1)
    c: Distance(g1) = 3
    c: Coincident(g2,g0)
    c: Vertical(g2)
    c: Distance(g2) = 3
    c: Coincident(g3,g1)
    c: Horizontal(g3)
    c: Distance(g3) = 3
    c: Coincident(g4,g2)
    c: Horizontal(g4)
    c: Distance(g4) = 3
    c: Vertical(g5)
    c: Vertical(g6)
    c: Coincident(g7,g6)
    c: Coincident(g7,g5)
    c: Weight(g8) = 1
    c: Equal(g8,g9)
    c: Equal(g8,g10)
    c: Coincident(g11,g4)
    c: InternalAlignment(g8,g11)
    c: InternalAlignment(g9,g11)
    c: InternalAlignment(g10,g11)
    c: InternalAlignment(g12,g11)
    c: InternalAlignment(g13,g11)
    c: Coincident(g17,g5)
    c: Weight(g14) = 1
    c: Equal(g14,g15)
    c: Equal(g14,g16)
    c: Coincident(g17,g3)
    c: InternalAlignment(g14,g17)
    c: InternalAlignment(g15,g17)
    c: InternalAlignment(g16,g17)
    c: InternalAlignment(g18,g17)
    c: InternalAlignment(g19,g17)
    c: Block(g7)
    c: Block(g17)
    c: Block(g11)
    c: Block(g6)
FEATURE [Part::Extrusion] Extrude003
  Base = -> Sketch002
  Dir = (0,0,1)
  DirMode = 2
  FaceMakerClass = Part::FaceMakerBullseye
  LengthFwd = 260
  LengthRev = 0
  Solid = true
  Symmetric = false
FEATURE [Part::Extrusion] Extrude
  Base = -> Sketch
  Dir = (0,0,1)
  DirMode = 2
  FaceMakerClass = Part::FaceMakerBullseye
  LengthFwd = 14
  LengthRev = 0
  Solid = true
  Symmetric = false
